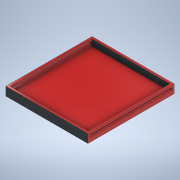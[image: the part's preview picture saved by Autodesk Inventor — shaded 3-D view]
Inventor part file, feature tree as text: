
AUTODESK INVENTOR PART (.ipt)
format: ipt  version: 2020 (Build 240168000, 168)  size: 175,104 bytes
history: native  units: in
note: dims shown in document units (in); Inventor stores cm internally (conversion verified against a paired STEP export)
features: extrude x7, sketch x7, plane x3
ambient origin geometry x8: Origin, YZ Plane, XZ Plane, XY Plane, X Axis, Y Axis, Z Axis, Center Point
bodies: Solid1 (feature_tree)
feature tree (17):
  extrude  "Extrusion1"  Depth=39.3701in
  extrude  "Extrusion2"  Depth=3.1496in
  extrude  "Extrusion3"  Depth=1.0in TaperAngle=0.0deg
  extrude  "Extrusion4"  Depth=3.1496in
  extrude  "Extrusion5"  Depth=39.3701in
  plane  "Work Plane1"
  extrude  "Extrusion6"  Depth=1.0in TaperAngle=0.0deg
  extrude  "Extrusion7"  Depth=1.1811in
  plane  "Work Plane2"
  plane  "Work Plane3"
  sketch  "Sketch1"  dims[d0=39.3701in d1=39.3701in]
  sketch  "Sketch2"  dims[d2=1.0in d3=0.0in d4=3.1496in]
  sketch  "Sketch3"  dims[d5=39.3701in d6=1.0in d7=0.0in]
  sketch  "Sketch4"  dims[d8=39.3701in d9=3.1496in]
  sketch  "Sketch5"  dims[d10=1.0in d11=0.0in d12=39.3701in]
  sketch  "Sketch6"  dims[d13=1.1811in d14=1.0in d15=0.0in]
  sketch  "Sketch7"  dims[d16=39.3701in d17=1.1811in d18=0.9843in d19=1.0in d20=0.0in d21=1.0in d22=0.0in d23=1.0in d24=0.0in d25=0.0in]
